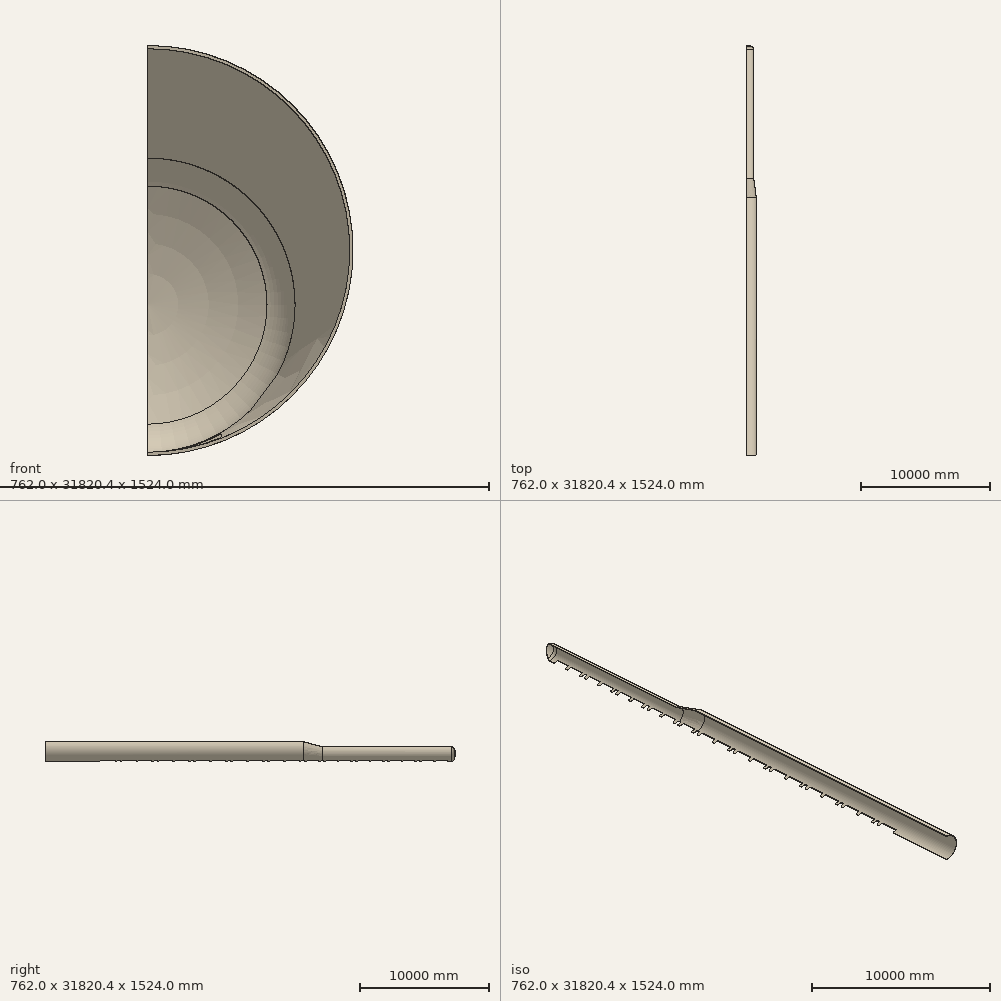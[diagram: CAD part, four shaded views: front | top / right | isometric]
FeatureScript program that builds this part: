
annotation { "Feature Type Name" : "Feature", "Feature Type Description" : "" }
export const myFeature = defineFeature(function(context is Context, id is Id, definition is map)
    precondition{}
    {
        {
            var Q0;
            Q0=qCreatedBy(makeId("Front.planeOp"),FACE);
            var sketch = newSketch(context, id + "F0", { "sketchPlane" : qUnion([Q0])});
            skCircle(sketch, "E0", {"center": v(0, 0) * mm, "radius": 762 * mm});
            skSolve(sketch);
        }
        {
            var Q0;
            Q0 = qSketchRegion(id + "F0", true);
            extrude(context, id + "F1", {"entities" : qUnion([Q0]), "oppositeDirection" : true, "depth" : 20000 * mm});
        }
        {
            var Q0;
            Q0=makeQuery(id+"F1.opExtrude","CAP_FACE",FACE,{"disambiguationData":[OSD([sQuery(id+"F0.wireOp",EDGE,"E0")])],"isStart":false});
            cPlane(context, id + "F2", {"entities" : qUnion([Q0]), "cplaneType" : CPlaneType.OFFSET, "offset" : 1500 * mm, "width" : 150 * mm, "height" : 150 * mm});
        }
        {
            var Q0;
            Q0=qCreatedBy(id+"F2.planeOp",FACE);
            var sketch = newSketch(context, id + "F3", { "sketchPlane" : qUnion([Q0])});
            skCircle(sketch, "E1", {"center": v(0, -203.2) * mm, "radius": 558.8 * mm});
            skSolve(sketch);
        }
        {
            var Q0;
            Q0 = qSketchRegion(id + "F3", true);
            extrude(context, id + "F4", {"entities" : qUnion([Q0]), "depth" : 10000 * mm});
        }
        {
            var Q0;
            Q0=makeQuery(id+"F1.opExtrude","CAP_FACE",FACE,{"disambiguationData":[OSD([sQuery(id+"F0.wireOp",EDGE,"E0")])],"isStart":false});
            var sketch = newSketch(context, id + "F5", { "sketchPlane" : qUnion([Q0])});
            skCircle(sketch, "E2", {"center": v(0, 0) * mm, "radius": 762 * mm});
            skSolve(sketch);
        }
        {
            var Q0;
            Q0 = qSketchRegion(id + "F5", true);
            var Q1;
            Q1 = qSketchRegion(id + "F3", true);
            loft(context, id + "F6", {"operationType" : NewBodyOperationType.ADD, "sheetProfilesArray" : [{ "sheetProfileEntities" : qUnion([Q0]) }, { "sheetProfileEntities" : qUnion([Q1]) }]});
        }
        {
            var Q0;
            Q0=makeQuery(id+"F1.opExtrude","CAP_FACE",FACE,{"disambiguationData":[OSD([sQuery(id+"F0.wireOp",EDGE,"E0")])],"isStart":true});
            var Q1;
            Q1=makeQuery(id+"F4.opExtrude","CAP_FACE",FACE,{"disambiguationData":[OSD([sQuery(id+"F3.wireOp",EDGE,"E1")])],"isStart":false});
            shell(context, id + "F7", {"entities" : qUnion([Q0, Q1]), "thickness" : 12 * mm});
        }
        {
            var Q0;
            Q0=qCreatedBy(makeId("Top.planeOp"),FACE);
            var sketch = newSketch(context, id + "F8", { "sketchPlane" : qUnion([Q0])});
            skLineSegment(sketch, "E3.bottom", {"start": v(-275, 4300) * mm, "end": v(275, 4300) * mm});
            skLineSegment(sketch, "E3.top", {"start": v(-275, 5400) * mm, "end": v(275, 5400) * mm});
            skLineSegment(sketch, "E3.left", {"start": v(-275, 4300) * mm, "end": v(-275, 5400) * mm});
            skLineSegment(sketch, "E3.right", {"start": v(275, 4300) * mm, "end": v(275, 5400) * mm});
            skLineSegment(sketch, "E4.bottom", {"start": v(-275, 5600) * mm, "end": v(275, 5600) * mm});
            skLineSegment(sketch, "E4.top", {"start": v(-275, 5800) * mm, "end": v(275, 5800) * mm});
            skLineSegment(sketch, "E4.left", {"start": v(-275, 5600) * mm, "end": v(-275, 5800) * mm});
            skLineSegment(sketch, "E4.right", {"start": v(275, 5600) * mm, "end": v(275, 5800) * mm});
            skLineSegment(sketch, "E5.bottom", {"start": v(-275, 6000) * mm, "end": v(275, 6000) * mm});
            skLineSegment(sketch, "E5.top", {"start": v(-275, 7030) * mm, "end": v(275, 7030) * mm});
            skLineSegment(sketch, "E5.left", {"start": v(-275, 6000) * mm, "end": v(-275, 7030) * mm});
            skLineSegment(sketch, "E5.right", {"start": v(275, 6000) * mm, "end": v(275, 7030) * mm});
            skLineSegment(sketch, "E6.bottom", {"start": v(-275, 7230) * mm, "end": v(275, 7230) * mm});
            skLineSegment(sketch, "E6.top", {"start": v(-275, 8260) * mm, "end": v(275, 8260) * mm});
            skLineSegment(sketch, "E6.left", {"start": v(-275, 7230) * mm, "end": v(-275, 8260) * mm});
            skLineSegment(sketch, "E6.right", {"start": v(275, 7230) * mm, "end": v(275, 8260) * mm});
            skLineSegment(sketch, "E7.0.1.0", {"start": v(-275, 11120) * mm, "end": v(275, 11120) * mm});
            skLineSegment(sketch, "E7.0.1.1", {"start": v(-275, 9890) * mm, "end": v(275, 9890) * mm});
            skLineSegment(sketch, "E7.0.1.2", {"start": v(-275, 10090) * mm, "end": v(-275, 11120) * mm});
            skLineSegment(sketch, "E7.0.1.3", {"start": v(-275, 8860) * mm, "end": v(-275, 9890) * mm});
            skLineSegment(sketch, "E7.0.1.4", {"start": v(275, 8860) * mm, "end": v(275, 9890) * mm});
            skLineSegment(sketch, "E7.0.1.5", {"start": v(-275, 10090) * mm, "end": v(275, 10090) * mm});
            skLineSegment(sketch, "E7.0.1.6", {"start": v(275, 10090) * mm, "end": v(275, 11120) * mm});
            skLineSegment(sketch, "E7.0.1.7", {"start": v(-275, 8860) * mm, "end": v(275, 8860) * mm});
            skLineSegment(sketch, "E7.0.2.0", {"start": v(-275, 13980) * mm, "end": v(275, 13980) * mm});
            skLineSegment(sketch, "E7.0.2.1", {"start": v(-275, 12750) * mm, "end": v(275, 12750) * mm});
            skLineSegment(sketch, "E7.0.2.2", {"start": v(-275, 12950) * mm, "end": v(-275, 13980) * mm});
            skLineSegment(sketch, "E7.0.2.3", {"start": v(-275, 11720) * mm, "end": v(-275, 12750) * mm});
            skLineSegment(sketch, "E7.0.2.4", {"start": v(275, 11720) * mm, "end": v(275, 12750) * mm});
            skLineSegment(sketch, "E7.0.2.5", {"start": v(-275, 12950) * mm, "end": v(275, 12950) * mm});
            skLineSegment(sketch, "E7.0.2.6", {"start": v(275, 12950) * mm, "end": v(275, 13980) * mm});
            skLineSegment(sketch, "E7.0.2.7", {"start": v(-275, 11720) * mm, "end": v(275, 11720) * mm});
            skLineSegment(sketch, "E7.0.3.0", {"start": v(-275, 16840) * mm, "end": v(275, 16840) * mm});
            skLineSegment(sketch, "E7.0.3.1", {"start": v(-275, 15610) * mm, "end": v(275, 15610) * mm});
            skLineSegment(sketch, "E7.0.3.2", {"start": v(-275, 15810) * mm, "end": v(-275, 16840) * mm});
            skLineSegment(sketch, "E7.0.3.3", {"start": v(-275, 14580) * mm, "end": v(-275, 15610) * mm});
            skLineSegment(sketch, "E7.0.3.4", {"start": v(275, 14580) * mm, "end": v(275, 15610) * mm});
            skLineSegment(sketch, "E7.0.3.5", {"start": v(-275, 15810) * mm, "end": v(275, 15810) * mm});
            skLineSegment(sketch, "E7.0.3.6", {"start": v(275, 15810) * mm, "end": v(275, 16840) * mm});
            skLineSegment(sketch, "E7.0.3.7", {"start": v(-275, 14580) * mm, "end": v(275, 14580) * mm});
            skLineSegment(sketch, "E7.0.4.0", {"start": v(-275, 19700) * mm, "end": v(275, 19700) * mm});
            skLineSegment(sketch, "E7.0.4.1", {"start": v(-275, 18470) * mm, "end": v(275, 18470) * mm});
            skLineSegment(sketch, "E7.0.4.2", {"start": v(-275, 18670) * mm, "end": v(-275, 19700) * mm});
            skLineSegment(sketch, "E7.0.4.3", {"start": v(-275, 17440) * mm, "end": v(-275, 18470) * mm});
            skLineSegment(sketch, "E7.0.4.4", {"start": v(275, 17440) * mm, "end": v(275, 18470) * mm});
            skLineSegment(sketch, "E7.0.4.5", {"start": v(-275, 18670) * mm, "end": v(275, 18670) * mm});
            skLineSegment(sketch, "E7.0.4.6", {"start": v(275, 18670) * mm, "end": v(275, 19700) * mm});
            skLineSegment(sketch, "E7.0.4.7", {"start": v(-275, 17440) * mm, "end": v(275, 17440) * mm});
            skLineSegment(sketch, "E7.direction1", {"start": v(-16599.33, 6000) * mm, "end": v(-275, 6000) * mm, "construction": true});
            skLineSegment(sketch, "E7.direction2", {"start": v(-275, 6000) * mm, "end": v(-275, 8860) * mm, "construction": true});
            skLineSegment(sketch, "E8.0.1.0", {"start": v(-275, 8460) * mm, "end": v(-275, 8660) * mm});
            skLineSegment(sketch, "E8.0.1.1", {"start": v(-275, 8660) * mm, "end": v(275, 8660) * mm});
            skLineSegment(sketch, "E8.0.1.2", {"start": v(-275, 8460) * mm, "end": v(275, 8460) * mm});
            skLineSegment(sketch, "E8.0.1.3", {"start": v(275, 8460) * mm, "end": v(275, 8660) * mm});
            skLineSegment(sketch, "E8.0.2.0", {"start": v(-275, 11320) * mm, "end": v(-275, 11520) * mm});
            skLineSegment(sketch, "E8.0.2.1", {"start": v(-275, 11520) * mm, "end": v(275, 11520) * mm});
            skLineSegment(sketch, "E8.0.2.2", {"start": v(-275, 11320) * mm, "end": v(275, 11320) * mm});
            skLineSegment(sketch, "E8.0.2.3", {"start": v(275, 11320) * mm, "end": v(275, 11520) * mm});
            skLineSegment(sketch, "E8.0.3.0", {"start": v(-275, 14180) * mm, "end": v(-275, 14380) * mm});
            skLineSegment(sketch, "E8.0.3.1", {"start": v(-275, 14380) * mm, "end": v(275, 14380) * mm});
            skLineSegment(sketch, "E8.0.3.2", {"start": v(-275, 14180) * mm, "end": v(275, 14180) * mm});
            skLineSegment(sketch, "E8.0.3.3", {"start": v(275, 14180) * mm, "end": v(275, 14380) * mm});
            skLineSegment(sketch, "E8.0.4.0", {"start": v(-275, 17040) * mm, "end": v(-275, 17240) * mm});
            skLineSegment(sketch, "E8.0.4.1", {"start": v(-275, 17240) * mm, "end": v(275, 17240) * mm});
            skLineSegment(sketch, "E8.0.4.2", {"start": v(-275, 17040) * mm, "end": v(275, 17040) * mm});
            skLineSegment(sketch, "E8.0.4.3", {"start": v(275, 17040) * mm, "end": v(275, 17240) * mm});
            skLineSegment(sketch, "E8.0.5.0", {"start": v(-275, 19900) * mm, "end": v(-275, 20100) * mm});
            skLineSegment(sketch, "E8.0.5.1", {"start": v(-275, 20100) * mm, "end": v(275, 20100) * mm});
            skLineSegment(sketch, "E8.0.5.2", {"start": v(-275, 19900) * mm, "end": v(275, 19900) * mm});
            skLineSegment(sketch, "E8.0.5.3", {"start": v(275, 19900) * mm, "end": v(275, 20100) * mm});
            skLineSegment(sketch, "E8.direction1", {"start": v(-16599.33, 5600) * mm, "end": v(-275, 5600) * mm, "construction": true});
            skLineSegment(sketch, "E8.direction2", {"start": v(-275, 5600) * mm, "end": v(-275, 8460) * mm, "construction": true});
            skLineSegment(sketch, "E9.bottom", {"start": v(-275, 20300) * mm, "end": v(275, 20300) * mm});
            skLineSegment(sketch, "E9.top", {"start": v(-275, 21200) * mm, "end": v(275, 21200) * mm});
            skLineSegment(sketch, "E9.left", {"start": v(-275, 20300) * mm, "end": v(-275, 21200) * mm});
            skLineSegment(sketch, "E9.right", {"start": v(275, 20300) * mm, "end": v(275, 21200) * mm});
            skLineSegment(sketch, "E10.bottom", {"start": v(-275, 21600) * mm, "end": v(275, 21600) * mm});
            skLineSegment(sketch, "E10.top", {"start": v(-275, 21400) * mm, "end": v(275, 21400) * mm});
            skLineSegment(sketch, "E10.left", {"start": v(-275, 21600) * mm, "end": v(-275, 21400) * mm});
            skLineSegment(sketch, "E10.right", {"start": v(275, 21600) * mm, "end": v(275, 21400) * mm});
            skLineSegment(sketch, "E11.bottom", {"start": v(-275, 21800) * mm, "end": v(275, 21800) * mm});
            skLineSegment(sketch, "E11.top", {"start": v(-275, 22640) * mm, "end": v(275, 22640) * mm});
            skLineSegment(sketch, "E11.left", {"start": v(-275, 21800) * mm, "end": v(-275, 22640) * mm});
            skLineSegment(sketch, "E11.right", {"start": v(275, 21800) * mm, "end": v(275, 22640) * mm});
            skLineSegment(sketch, "E12.bottom", {"start": v(-275, 22840) * mm, "end": v(275, 22840) * mm});
            skLineSegment(sketch, "E12.top", {"start": v(-275, 23680) * mm, "end": v(275, 23680) * mm});
            skLineSegment(sketch, "E12.left", {"start": v(-275, 22840) * mm, "end": v(-275, 23680) * mm});
            skLineSegment(sketch, "E12.right", {"start": v(275, 22840) * mm, "end": v(275, 23680) * mm});
            skLineSegment(sketch, "E13.0.1.0", {"start": v(-275, 26160) * mm, "end": v(275, 26160) * mm});
            skLineSegment(sketch, "E13.0.1.1", {"start": v(275, 24280) * mm, "end": v(275, 25120) * mm});
            skLineSegment(sketch, "E13.0.1.2", {"start": v(-275, 25320) * mm, "end": v(275, 25320) * mm});
            skLineSegment(sketch, "E13.0.1.3", {"start": v(-275, 25320) * mm, "end": v(-275, 26160) * mm});
            skLineSegment(sketch, "E13.0.1.4", {"start": v(-275, 24280) * mm, "end": v(275, 24280) * mm});
            skLineSegment(sketch, "E13.0.1.5", {"start": v(-275, 24280) * mm, "end": v(-275, 25120) * mm});
            skLineSegment(sketch, "E13.0.1.6", {"start": v(-275, 25120) * mm, "end": v(275, 25120) * mm});
            skLineSegment(sketch, "E13.0.1.7", {"start": v(275, 25320) * mm, "end": v(275, 26160) * mm});
            skLineSegment(sketch, "E13.0.2.0", {"start": v(-275, 28640) * mm, "end": v(275, 28640) * mm});
            skLineSegment(sketch, "E13.0.2.1", {"start": v(275, 26760) * mm, "end": v(275, 27600) * mm});
            skLineSegment(sketch, "E13.0.2.2", {"start": v(-275, 27800) * mm, "end": v(275, 27800) * mm});
            skLineSegment(sketch, "E13.0.2.3", {"start": v(-275, 27800) * mm, "end": v(-275, 28640) * mm});
            skLineSegment(sketch, "E13.0.2.4", {"start": v(-275, 26760) * mm, "end": v(275, 26760) * mm});
            skLineSegment(sketch, "E13.0.2.5", {"start": v(-275, 26760) * mm, "end": v(-275, 27600) * mm});
            skLineSegment(sketch, "E13.0.2.6", {"start": v(-275, 27600) * mm, "end": v(275, 27600) * mm});
            skLineSegment(sketch, "E13.0.2.7", {"start": v(275, 27800) * mm, "end": v(275, 28640) * mm});
            skLineSegment(sketch, "E13.direction1", {"start": v(-15568.68, 21800) * mm, "end": v(-275, 21800) * mm, "construction": true});
            skLineSegment(sketch, "E13.direction2", {"start": v(-275, 21800) * mm, "end": v(-275, 24280) * mm, "construction": true});
            skLineSegment(sketch, "E14.bottom", {"start": v(-275, 24080) * mm, "end": v(275, 24080) * mm});
            skLineSegment(sketch, "E14.top", {"start": v(-275, 23880) * mm, "end": v(275, 23880) * mm});
            skLineSegment(sketch, "E14.left", {"start": v(-275, 24080) * mm, "end": v(-275, 23880) * mm});
            skLineSegment(sketch, "E14.right", {"start": v(275, 24080) * mm, "end": v(275, 23880) * mm});
            skLineSegment(sketch, "E15.bottom", {"start": v(-275, 26560) * mm, "end": v(275, 26560) * mm});
            skLineSegment(sketch, "E15.top", {"start": v(-275, 26360) * mm, "end": v(275, 26360) * mm});
            skLineSegment(sketch, "E15.left", {"start": v(-275, 26560) * mm, "end": v(-275, 26360) * mm});
            skLineSegment(sketch, "E15.right", {"start": v(275, 26560) * mm, "end": v(275, 26360) * mm});
            skLineSegment(sketch, "E16.bottom", {"start": v(-275, 29040) * mm, "end": v(275, 29040) * mm});
            skLineSegment(sketch, "E16.top", {"start": v(-275, 28840) * mm, "end": v(275, 28840) * mm});
            skLineSegment(sketch, "E16.left", {"start": v(-275, 29040) * mm, "end": v(-275, 28840) * mm});
            skLineSegment(sketch, "E16.right", {"start": v(275, 29040) * mm, "end": v(275, 28840) * mm});
            skLineSegment(sketch, "E17.bottom", {"start": v(-275, 29240) * mm, "end": v(275, 29240) * mm});
            skLineSegment(sketch, "E17.top", {"start": v(-275, 30120) * mm, "end": v(275, 30120) * mm});
            skLineSegment(sketch, "E17.left", {"start": v(-275, 29240) * mm, "end": v(-275, 30120) * mm});
            skLineSegment(sketch, "E17.right", {"start": v(275, 29240) * mm, "end": v(275, 30120) * mm});
            skLineSegment(sketch, "E18.bottom", {"start": v(-275, 31200) * mm, "end": v(275, 31200) * mm});
            skLineSegment(sketch, "E18.top", {"start": v(-275, 30320) * mm, "end": v(275, 30320) * mm});
            skLineSegment(sketch, "E18.left", {"start": v(-275, 31200) * mm, "end": v(-275, 30320) * mm});
            skLineSegment(sketch, "E18.right", {"start": v(275, 31200) * mm, "end": v(275, 30320) * mm});
            skSolve(sketch);
        }
        {
            var Q0;
            Q0 = qSketchRegion(id + "F8", true);
            extrude(context, id + "F9", {"entities" : qUnion([Q0]), "operationType" : NewBodyOperationType.REMOVE, "endBound" : BoundingType.THROUGH_ALL, "oppositeDirection" : true, "depth" : 25 * mm});
        }
        {
            var Q0;
            Q0=qCreatedBy(makeId("Right.planeOp"),FACE);
            var sketch = newSketch(context, id + "F10", { "sketchPlane" : qUnion([Q0])});
            skLineSegment(sketch, "E19", {"start": v(31500, 343.6) * mm, "end": v(31535, 343.6) * mm});
            skArc(sketch, "E20", {"start": v(31535, 343.6) * mm, "mid": v(31634.29, 315.4) * mm, "end": v(31703.92, 239.2) * mm});
            skArc(sketch, "E21", {"start": v(31703.92, 239.2) * mm, "mid": v(31781.9, 24.09) * mm, "end": v(31808.37, -203.2) * mm});
            skLineSegment(sketch, "E22", {"start": v(30753.4, -203.2) * mm, "end": v(31500, -203.2) * mm, "construction": true});
            skArc(sketch, "E23.0", {"start": v(31714.65, 244.58) * mm, "mid": v(31793.58, 26.84) * mm, "end": v(31820.37, -203.2) * mm});
            skArc(sketch, "E23.1", {"start": v(31535, 355.6) * mm, "mid": v(31640.6, 325.6) * mm, "end": v(31714.65, 244.58) * mm});
            skLineSegment(sketch, "E23.2", {"start": v(31500, 355.6) * mm, "end": v(31535, 355.6) * mm});
            skLineSegment(sketch, "E24", {"start": v(31500, 343.6) * mm, "end": v(31500, 355.6) * mm});
            skLineSegment(sketch, "E25", {"start": v(31808.37, -203.2) * mm, "end": v(31820.37, -203.2) * mm});
            skSolve(sketch);
        }
        {
            var Q0;
            Q0 = qSketchRegion(id + "F10", true);
            var Q1;
            Q1=sQuery(id+"F10.wireOp",EDGE,"E22");
            revolve(context, id + "F11", {"operationType" : NewBodyOperationType.ADD, "entities" : qUnion([Q0]), "axis" : qUnion([Q1]), "revolveType" : RevolveType.ONE_DIRECTION, "angle" : 180 * degree});
        }
        {
            var Q0;
            Q0=qCreatedBy(makeId("Top.planeOp"),FACE);
            var sketch = newSketch(context, id + "F12", { "sketchPlane" : qUnion([Q0])});
            skLineSegment(sketch, "E26.bottom", {"start": v(-8196.82, 32307.43) * mm, "end": v(0, 32307.43) * mm});
            skLineSegment(sketch, "E26.top", {"start": v(-8196.82, 0) * mm, "end": v(0, 0) * mm});
            skLineSegment(sketch, "E26.left", {"start": v(-8196.82, 32307.43) * mm, "end": v(-8196.82, 0) * mm});
            skLineSegment(sketch, "E26.right", {"start": v(0, 32307.43) * mm, "end": v(0, 0) * mm});
            skSolve(sketch);
        }
        {
            var Q0;
            Q0 = qSketchRegion(id + "F12", true);
            extrude(context, id + "F13", {"entities" : qUnion([Q0]), "operationType" : NewBodyOperationType.REMOVE, "endBound" : BoundingType.THROUGH_ALL, "depth" : 25 * mm, "hasSecondDirection" : true, "secondDirectionBound" : SecondDirectionBoundingType.THROUGH_ALL, "secondDirectionOppositeDirection" : true, "secondDirectionDepth" : 25 * mm});
        }
    });
